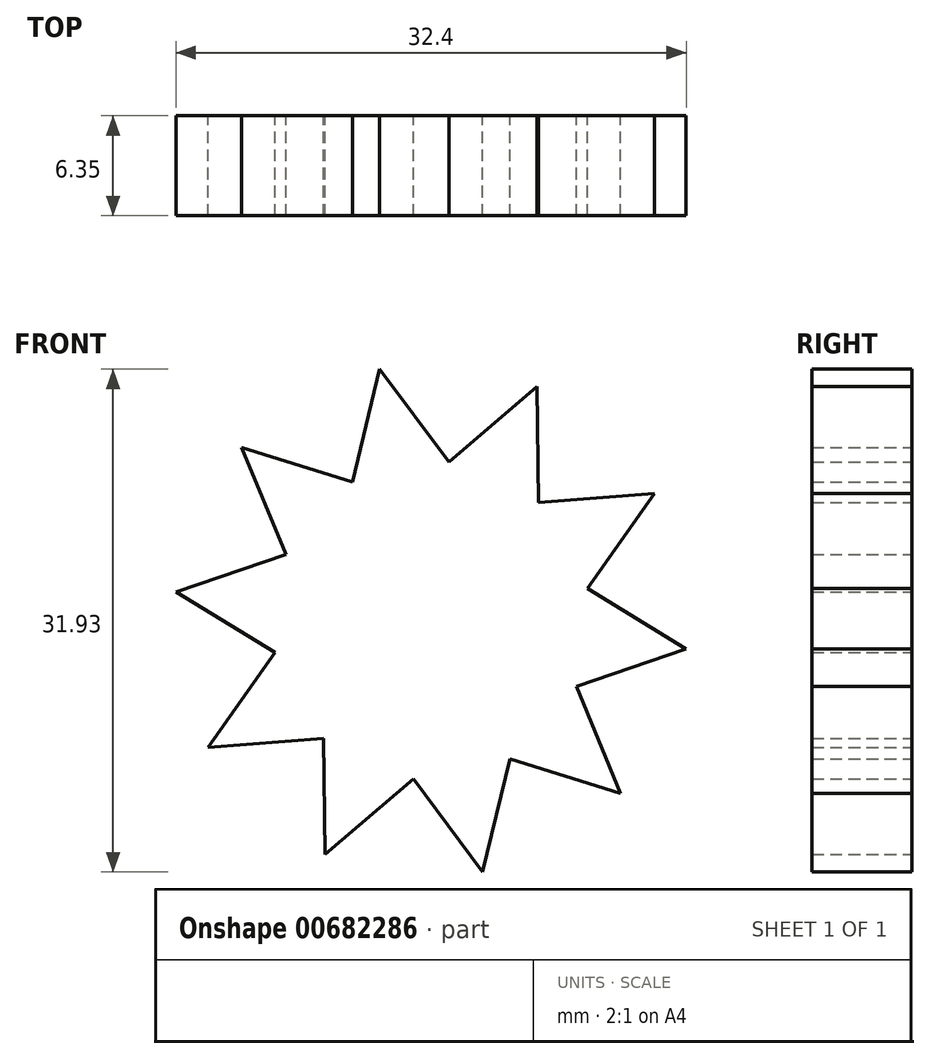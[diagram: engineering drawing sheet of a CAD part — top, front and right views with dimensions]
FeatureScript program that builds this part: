
annotation { "Feature Type Name" : "Feature", "Feature Type Description" : "" }
export const myFeature = defineFeature(function(context is Context, id is Id, definition is map)
    precondition{}
    {
        {
            var Q0;
            Q0=qCreatedBy(makeId("Front.planeOp"),FACE);
            var sketch = newSketch(context, id + "F0", { "sketchPlane" : qUnion([Q0])});
            skCircle(sketch, "E0.cCircle", {"center": v(0.24, 0.9) * mm, "radius": 9.63 * mm, "construction": true});
            skLineSegment(sketch, "E0.0", {"start": v(-6.6, -6.59) * mm, "end": v(-9.69, -1.14) * mm});
            skLineSegment(sketch, "E0.1", {"start": v(-9.69, -1.14) * mm, "end": v(-8.99, 5.08) * mm});
            skLineSegment(sketch, "E0.2", {"start": v(-8.99, 5.08) * mm, "end": v(-4.77, 9.7) * mm});
            skLineSegment(sketch, "E0.3", {"start": v(-4.77, 9.7) * mm, "end": v(1.36, 10.96) * mm});
            skLineSegment(sketch, "E0.4", {"start": v(1.36, 10.96) * mm, "end": v(7.07, 8.38) * mm});
            skLineSegment(sketch, "E0.5", {"start": v(7.07, 8.38) * mm, "end": v(10.16, 2.93) * mm});
            skLineSegment(sketch, "E0.6", {"start": v(10.16, 2.93) * mm, "end": v(9.46, -3.29) * mm});
            skLineSegment(sketch, "E0.7", {"start": v(9.46, -3.29) * mm, "end": v(5.24, -7.91) * mm});
            skLineSegment(sketch, "E0.8", {"start": v(5.24, -7.91) * mm, "end": v(-0.9, -9.17) * mm});
            skLineSegment(sketch, "E0.9", {"start": v(-0.9, -9.17) * mm, "end": v(-6.6, -6.59) * mm});
            skPoint(sketch, "E0.0.midPoint", {"position": v(-8.14, -3.87) * mm});
            skLineSegment(sketch, "E1", {"start": v(-4.77, 9.7) * mm, "end": v(-3.04, 16.86) * mm});
            skLineSegment(sketch, "E2", {"start": v(-3.04, 16.86) * mm, "end": v(1.36, 10.96) * mm});
            skLineSegment(sketch, "E3", {"start": v(1.36, 10.96) * mm, "end": v(6.97, 15.74) * mm});
            skLineSegment(sketch, "E4", {"start": v(6.97, 15.74) * mm, "end": v(7.07, 8.38) * mm});
            skLineSegment(sketch, "E5", {"start": v(-8.99, 5.08) * mm, "end": v(-11.8, 11.89) * mm});
            skLineSegment(sketch, "E6", {"start": v(-11.8, 11.89) * mm, "end": v(-4.77, 9.7) * mm});
            skLineSegment(sketch, "E7", {"start": v(-8.99, 5.08) * mm, "end": v(-15.96, 2.71) * mm});
            skLineSegment(sketch, "E8", {"start": v(-15.96, 2.71) * mm, "end": v(-9.69, -1.14) * mm});
            skLineSegment(sketch, "E9", {"start": v(-9.69, -1.14) * mm, "end": v(-13.94, -7.16) * mm});
            skLineSegment(sketch, "E10", {"start": v(-13.94, -7.16) * mm, "end": v(-6.6, -6.59) * mm});
            skLineSegment(sketch, "E11", {"start": v(-6.6, -6.59) * mm, "end": v(-6.5, -13.95) * mm});
            skLineSegment(sketch, "E12", {"start": v(-6.5, -13.95) * mm, "end": v(-0.9, -9.17) * mm});
            skLineSegment(sketch, "E13", {"start": v(-0.9, -9.17) * mm, "end": v(3.52, -15.07) * mm});
            skLineSegment(sketch, "E14", {"start": v(3.52, -15.07) * mm, "end": v(5.24, -7.91) * mm});
            skLineSegment(sketch, "E15", {"start": v(5.24, -7.91) * mm, "end": v(12.28, -10.1) * mm});
            skLineSegment(sketch, "E16", {"start": v(12.28, -10.1) * mm, "end": v(9.46, -3.29) * mm});
            skLineSegment(sketch, "E17", {"start": v(9.46, -3.29) * mm, "end": v(16.44, -0.92) * mm});
            skLineSegment(sketch, "E18", {"start": v(16.44, -0.92) * mm, "end": v(10.16, 2.93) * mm});
            skLineSegment(sketch, "E19", {"start": v(10.16, 2.93) * mm, "end": v(14.41, 8.95) * mm});
            skLineSegment(sketch, "E20", {"start": v(14.41, 8.95) * mm, "end": v(7.07, 8.38) * mm});
            skSolve(sketch);
        }
        {
            var Q0;
            Q0 = qSketchRegion(id + "F0", true);
            extrude(context, id + "F1", {"entities" : qUnion([Q0]), "depth" : 6.35 * mm, "offsetDistance" : 25.4 * mm});
        }
    });
